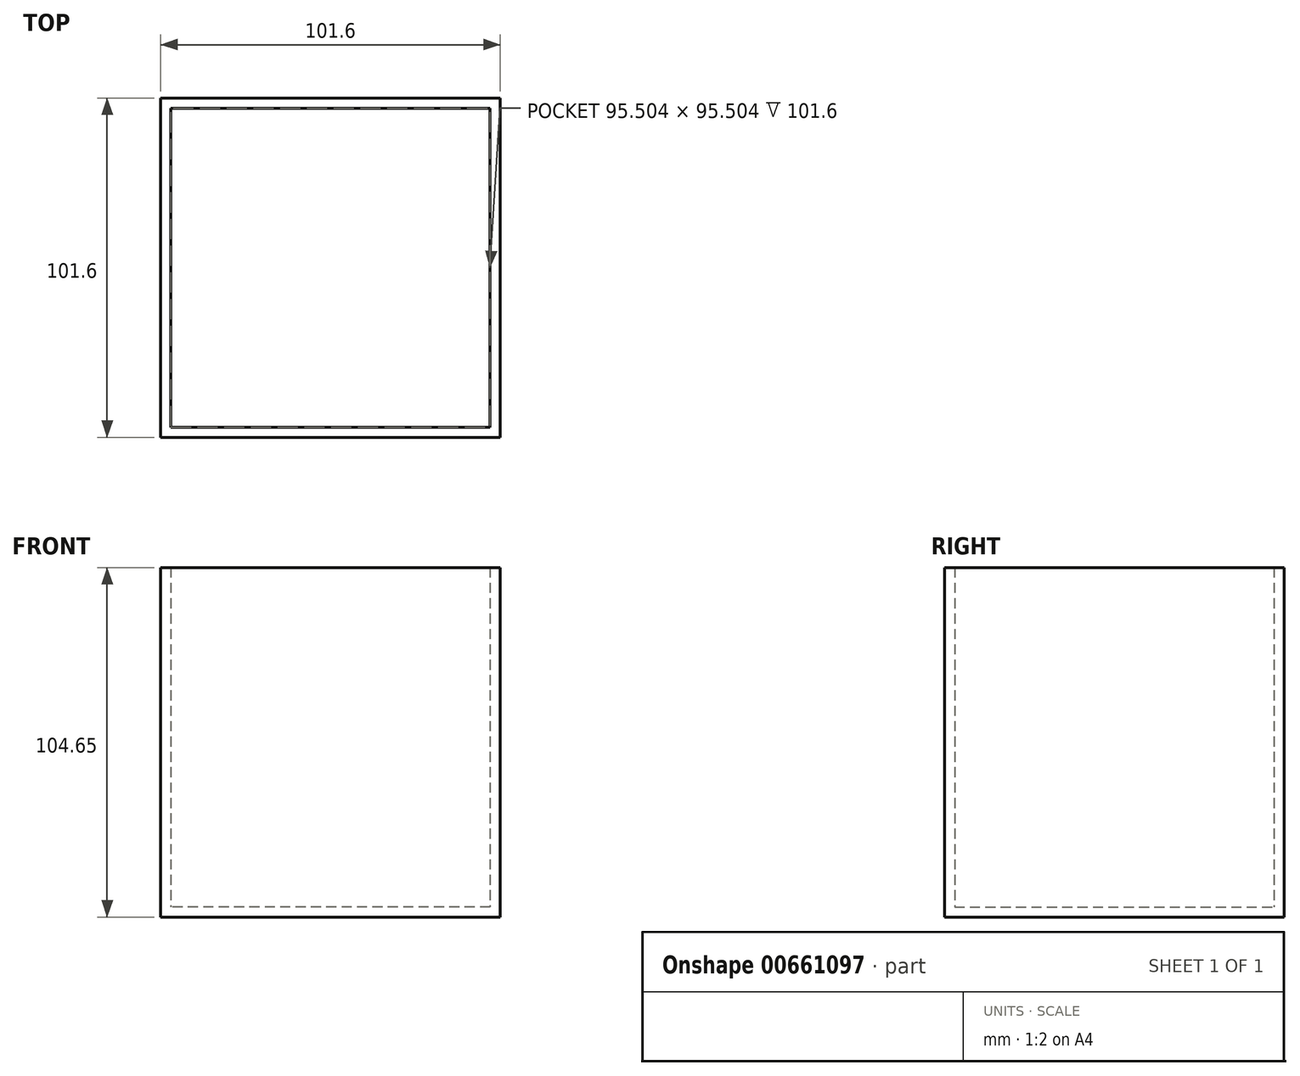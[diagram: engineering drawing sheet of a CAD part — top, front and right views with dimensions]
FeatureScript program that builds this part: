
annotation { "Feature Type Name" : "Feature", "Feature Type Description" : "" }
export const myFeature = defineFeature(function(context is Context, id is Id, definition is map)
    precondition{}
    {
        {
            var Q0;
            Q0=qCreatedBy(makeId("Top.planeOp"),FACE);
            var sketch = newSketch(context, id + "F0", { "sketchPlane" : qUnion([Q0])});
            skLineSegment(sketch, "E0.bottom", {"start": v(50.8, -50.8) * mm, "end": v(-50.8, -50.8) * mm});
            skLineSegment(sketch, "E0.top", {"start": v(50.8, 50.8) * mm, "end": v(-50.8, 50.8) * mm});
            skLineSegment(sketch, "E0.left", {"start": v(50.8, -50.8) * mm, "end": v(50.8, 50.8) * mm});
            skLineSegment(sketch, "E0.right", {"start": v(-50.8, -50.8) * mm, "end": v(-50.8, 50.8) * mm});
            skPoint(sketch, "E0.middle", {"position": v(0, 0) * mm});
            skSolve(sketch);
        }
        {
            var Q0;
            Q0 = qSketchRegion(id + "F0", true);
            extrude(context, id + "F1", {"entities" : qUnion([Q0]), "depth" : 3.05 * mm, "offsetDistance" : 25.4 * mm});
        }
        {
            var Q0;
            Q0=makeQuery(id+"F1.opExtrude","CAP_FACE",FACE,{"disambiguationData":[OSD([sQuery(id+"F0.wireOp",EDGE,"E0.bottom"),sQuery(id+"F0.wireOp",EDGE,"E0.top"),sQuery(id+"F0.wireOp",EDGE,"E0.left"),sQuery(id+"F0.wireOp",EDGE,"E0.right")])],"isStart":false});
            var sketch = newSketch(context, id + "F2", { "sketchPlane" : qUnion([Q0])});
            skLineSegment(sketch, "E1.0", {"start": v(47.75, -47.75) * mm, "end": v(-47.75, -47.75) * mm});
            skLineSegment(sketch, "E1.1", {"start": v(47.75, -47.75) * mm, "end": v(47.75, 47.75) * mm});
            skLineSegment(sketch, "E1.2", {"start": v(47.75, 47.75) * mm, "end": v(-47.75, 47.75) * mm});
            skLineSegment(sketch, "E1.3", {"start": v(-47.75, -47.75) * mm, "end": v(-47.75, 47.75) * mm});
            skSolve(sketch);
        }
        {
            var Q0;
            Q0=makeQuery(id+"F2.imprint","IMPRINT",FACE,{"disambiguationData":[TD([[makeQuery(id+"F2.imprint","IMPRINT",EDGE,{"derivedFrom":sQuery(id+"F2.wireOp",EDGE,"E1.0")}),1.0]])]});
            extrude(context, id + "F3", {"entities" : qUnion([Q0]), "operationType" : NewBodyOperationType.ADD, "depth" : 101.6 * mm, "offsetDistance" : 25.4 * mm});
        }
    });
